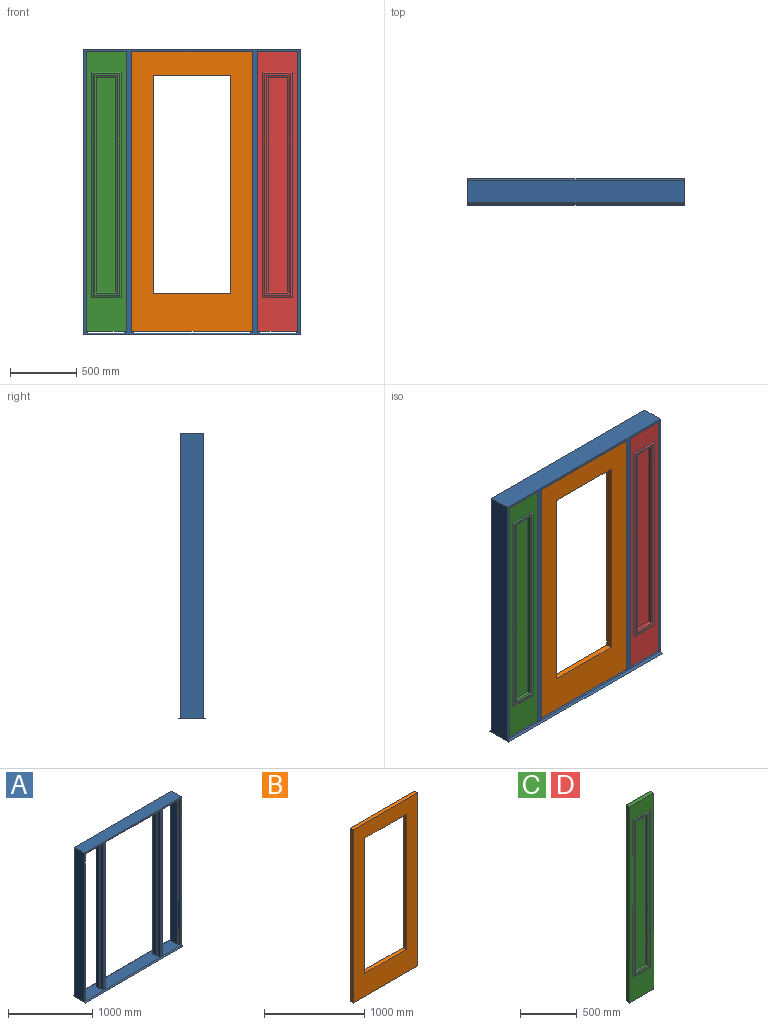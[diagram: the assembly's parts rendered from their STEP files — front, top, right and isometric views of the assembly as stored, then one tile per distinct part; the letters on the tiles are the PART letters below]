
ASSEMBLY  parts=4 mates=4
PART A: 30 faces, bbox 1638.3x203.2x2162.2 mm
  f0: plane 1638.3x203.2mm, normal (0,0,-1), area 332902.6mm2, adj f15,f18,f19,f29
  f1: plane 1638.3x168.28mm, normal (0,0,1), area 275684.9mm2, adj f14,f15,f16,f29
  f2: plane 914.4x46.04mm, normal (0,0,-1), area 42096.7mm2, adj f12,f13,f16,f28
  f3: plane 1574.8x122.24mm, normal (0,0,-1), area 184233.5mm2, adj f6,f7,f8,f9,f10,f13,f14,f22
  f4: plane 304.8x46.04mm, normal (0,0,-1), area 14032.2mm2, adj f5,f7,f11,f16
  f5: plane 2130.43x46.04mm, normal (-1,0,0), area 98079.4mm2, adj f4,f7,f16,f17
  f6: plane 2117.73x122.24mm, normal (-1,0,0), area 258865.4mm2, adj f3,f7,f14,f17
  f7: plane 2130.43x304.8mm, normal (0,-1,0), area 57661.2mm2, adj f3,f4,f5,f6,f10,f11,f17
  f8: plane 2117.73x65.09mm, normal (-1,0,0), area 137837.4mm2, adj f3,f9,f13,f17
  f9: plane 2117.73x63.5mm, normal (0,1,0), area 134475.5mm2, adj f3,f8,f10,f17
  f10: plane 2117.73x65.09mm, normal (1,0,0), area 137837.4mm2, adj f3,f7,f9,f17
  f11: plane 2130.43x46.04mm, normal (1,0,0), area 98079.4mm2, adj f4,f7,f16,f17
  f12: plane 2130.43x46.04mm, normal (-1,0,0), area 98079.4mm2, adj f2,f13,f16,f17
  f13: plane 2130.43x914.4mm, normal (0,-1,0), area 65403.1mm2, adj f2,f3,f8,f12,f17,f24,f28
  f14: plane 2149.48x1638.3mm, normal (0,1,0), area 186491.6mm2, adj f1,f3,f6,f15,f17,f22,f29
  f15: plane 2162.18x203.2mm, normal (1,0,0), area 364081.9mm2, adj f0,f1,f14,f16,f17,f18,f19
  f16: plane 2149.48x1638.3mm, normal (0,-1,0), area 274717.2mm2, adj f1,f2,f4,f5,f11,f12,f15,f17
  f17: plane 1638.3x171.45mm, normal (0,0,1), area 259596.3mm2, adj f5,f6,f7,f8,f9,f10,f11,f12
  f18: plane 1638.3x15.88mm, normal (0,-0.62,0.78), area 33306.5mm2, adj f0,f15,f17,f29
  f19: plane 1638.3x15.88mm, normal (0,0.62,0.78), area 33306.5mm2, adj f0,f15,f17,f29
  f20: plane 304.8x46.04mm, normal (0,0,-1), area 14032.2mm2, adj f16,f21,f23,f27
  f21: plane 2130.43x46.04mm, normal (1,0,0), area 98079.4mm2, adj f16,f17,f20,f23
  f22: plane 2117.73x122.24mm, normal (1,0,0), area 258865.4mm2, adj f3,f14,f17,f23
  f23: plane 2130.43x304.8mm, normal (0,-1,0), area 57661.2mm2, adj f3,f17,f20,f21,f22,f26,f27
  f24: plane 2117.73x65.09mm, normal (1,0,0), area 137837.4mm2, adj f3,f13,f17,f25
  f25: plane 2117.73x63.5mm, normal (0,1,0), area 134475.5mm2, adj f3,f17,f24,f26
  f26: plane 2117.73x65.09mm, normal (-1,0,0), area 137837.4mm2, adj f3,f17,f23,f25
  f27: plane 2130.43x46.04mm, normal (-1,0,0), area 98079.4mm2, adj f16,f17,f20,f23
  f28: plane 2130.43x46.04mm, normal (1,0,0), area 98079.4mm2, adj f2,f13,f16,f17
  f29: plane 2162.18x203.2mm, normal (-1,0,0), area 364081.9mm2, adj f0,f1,f14,f16,f17,f18,f19
PART B: 10 faces, bbox 907.3x44.5x2114.6 mm
  f0: plane 2114.55x907.26mm, normal (0,1,0), area 953924.5mm2, adj f2,f3,f4,f5,f6,f7,f8,f9
  f1: plane 2114.55x907.26mm, normal (0,-1,0), area 953924.5mm2, adj f2,f3,f4,f5,f6,f7,f8,f9
  f2: plane 2114.55x44.45mm, normal (1,0,0), area 93991.7mm2, adj f0,f1,f4,f5
  f3: plane 2114.55x44.45mm, normal (-1,0,0), area 93991.7mm2, adj f0,f1,f4,f5
  f4: plane 907.26x44.45mm, normal (0,0,1), area 40327.5mm2, adj f0,f1,f2,f3
  f5: plane 907.26x44.45mm, normal (0,0,-1), area 40327.5mm2, adj f0,f1,f2,f3
  f6: plane 584.2x44.45mm, normal (0,0,-1), area 25967.7mm2, adj f0,f1,f7,f9
  f7: plane 1651x44.45mm, normal (1,0,0), area 73386.9mm2, adj f0,f1,f6,f8
  f8: plane 584.2x44.45mm, normal (0,0,1), area 25967.7mm2, adj f0,f1,f7,f9
  f9: plane 1651x44.45mm, normal (-1,0,0), area 73386.9mm2, adj f0,f1,f6,f8
PART C: 34 faces, bbox 301.6x57.2x2114.6 mm
  f0: plane 2114.55x301.63mm, normal (0,1,0), area 259576.1mm2, adj f2,f3,f4,f5,f24,f27,f29,f32
  f1: plane 2114.55x301.63mm, normal (0,-1,0), area 259576.1mm2, adj f2,f3,f4,f5,f16,f17,f18,f19
  f2: plane 2114.55x44.45mm, normal (1,0,0), area 93991.7mm2, adj f0,f1,f4,f5
  f3: plane 2114.55x44.45mm, normal (-1,0,0), area 93991.7mm2, adj f0,f1,f4,f5
  f4: plane 301.63x44.45mm, normal (0,0,1), area 13407.2mm2, adj f0,f1,f2,f3
  f5: plane 301.63x44.45mm, normal (0,0,-1), area 13407.2mm2, adj f0,f1,f2,f3
  f6: plane 1625.6x146.05mm, normal (0,-1,0), area 237418.9mm2, adj f7,f8,f9,f10
  f7: plane 1625.6x25.4mm, normal (1,0,0), area 41290.2mm2, adj f6,f8,f10,f11
  f8: plane 146.05x25.4mm, normal (0,0,1), area 3709.7mm2, adj f6,f7,f9,f12
  f9: plane 1625.6x25.4mm, normal (-1,0,0), area 41290.2mm2, adj f6,f8,f10,f13
  f10: plane 146.05x25.4mm, normal (0,0,-1), area 3709.7mm2, adj f6,f7,f9,f14
  f11: plane 1651x12.7mm, normal (0.45,-0.89,0), area 23262.3mm2, adj f7,f12,f14,f15
  f12: plane 171.45x12.7mm, normal (0,-0.89,0.45), area 2254.1mm2, adj f8,f11,f13,f15
  f13: plane 1651x12.7mm, normal (-0.45,-0.89,0), area 23262.3mm2, adj f9,f12,f14,f15
  f14: plane 171.45x12.7mm, normal (0,-0.89,-0.45), area 2254.1mm2, adj f10,f11,f13,f15
  f15: plane 1676.4x196.85mm, normal (0,-1,0), area 46935.4mm2, adj f11,f12,f13,f14,f16,f17,f18,f19
  f16: plane 1701.8x12.7mm, normal (-0.45,-0.89,0), area 23983.6mm2, adj f1,f15,f17,f19
  f17: plane 222.25x12.7mm, normal (0,-0.89,-0.45), area 2975.4mm2, adj f1,f15,f16,f18
  f18: plane 1701.8x12.7mm, normal (0.45,-0.89,0), area 23983.6mm2, adj f1,f15,f17,f19
  f19: plane 222.25x12.7mm, normal (0,-0.89,0.45), area 2975.4mm2, adj f1,f15,f16,f18
  f20: plane 146.05x12.7mm, normal (0,0,-1), area 1854.8mm2, adj f21,f22,f30,f33
  f21: plane 1625.6x12.7mm, normal (-1,0,0), area 20645.1mm2, adj f20,f26,f28,f33
  f22: plane 171.45x12.7mm, normal (0,0.89,-0.45), area 2254.1mm2, adj f20,f23,f28,f31
  f23: plane 1676.4x196.85mm, normal (0,1,0), area 46935.4mm2, adj f22,f24,f25,f27,f28,f29,f31,f32
  f24: plane 222.25x12.7mm, normal (0,0.89,0.45), area 2975.4mm2, adj f0,f23,f29,f32
  f25: plane 171.45x12.7mm, normal (0,0.89,0.45), area 2254.1mm2, adj f23,f26,f28,f31
  f26: plane 146.05x12.7mm, normal (0,0,1), area 1854.8mm2, adj f21,f25,f30,f33
  f27: plane 222.25x12.7mm, normal (0,0.89,-0.45), area 2975.4mm2, adj f0,f23,f29,f32
  f28: plane 1651x12.7mm, normal (-0.45,0.89,0), area 23262.3mm2, adj f21,f22,f23,f25
  f29: plane 1701.8x12.7mm, normal (0.45,0.89,0), area 23983.6mm2, adj f0,f23,f24,f27
  f30: plane 1625.6x12.7mm, normal (1,0,0), area 20645.1mm2, adj f20,f26,f31,f33
  f31: plane 1651x12.7mm, normal (0.45,0.89,0), area 23262.3mm2, adj f22,f23,f25,f30
  f32: plane 1701.8x12.7mm, normal (-0.45,0.89,0), area 23983.6mm2, adj f0,f23,f24,f27
  f33: plane 1625.6x146.05mm, normal (0,1,0), area 237418.9mm2, adj f20,f21,f26,f30
PART D: same geometry as C
PLACE A t=(1757.2,-75.5,-36.35)mm fixed
PLACE B t=(1734.58,-74.71,-20.48)mm
PLACE C t=(784.06,-74.71,-20.48)mm
PLACE D t=(2079.46,-74.71,-20.48)mm
MATE fastened A.f4 <-> D.f4  axis (0,0,-1) through (1928.65,-52.49,2094.07)mm
MATE fastened A.f20 <-> C.f4  axis (0,0,-1) through (633.25,-52.49,2094.07)mm
MATE planar A.f20 <-> C.f4  axis (0,0,-1) through (633.25,-52.49,2094.07)mm
MATE fastened A.f2 <-> B.f4  axis (0,0,-1) through (1280.95,-52.49,2094.07)mm
